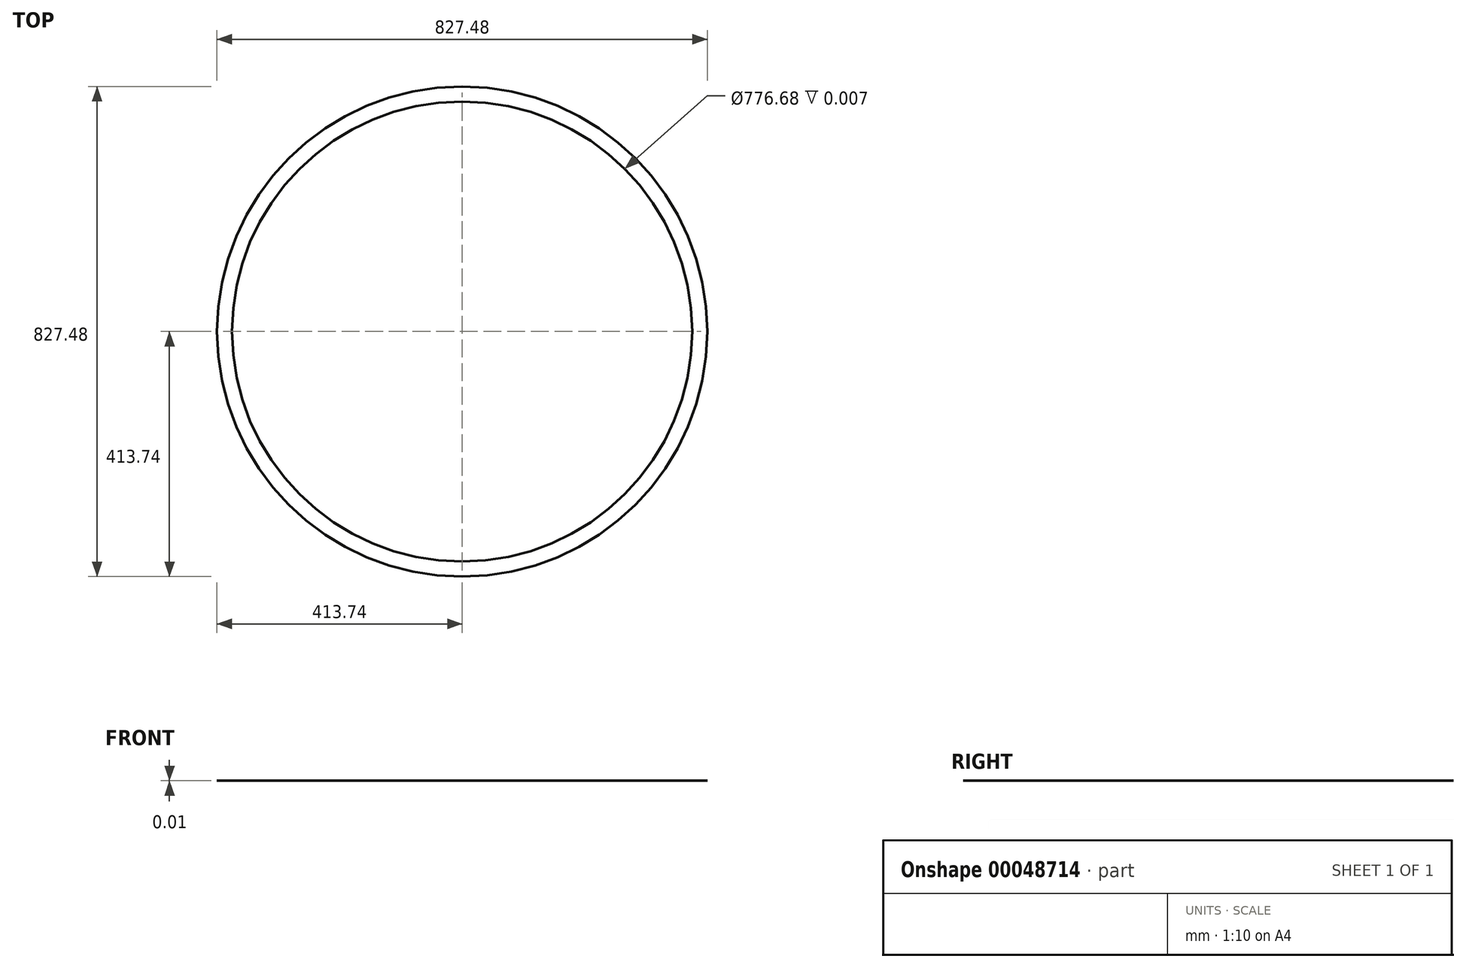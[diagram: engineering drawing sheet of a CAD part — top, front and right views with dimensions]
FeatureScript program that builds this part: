
annotation { "Feature Type Name" : "Feature", "Feature Type Description" : "" }
export const myFeature = defineFeature(function(context is Context, id is Id, definition is map)
    precondition{}
    {
        {
            var Q0;
            Q0=qCreatedBy(makeId("Top.planeOp"),FACE);
            var sketch = newSketch(context, id + "F0", { "sketchPlane" : qUnion([Q0])});
            skCircle(sketch, "E0", {"center": v(0, 0) * mm, "radius": 413.74 * mm});
            skCircle(sketch, "E1", {"center": v(0, 0) * mm, "radius": 388.34 * mm});
            skSolve(sketch);
        }
        {
            var Q0;
            Q0=makeQuery(id+"F0.imprint","IMPRINT",FACE,{"disambiguationData":[TD([[makeQuery(id+"F0.imprint","IMPRINT",EDGE,{"derivedFrom":sQuery(id+"F0.wireOp",EDGE,"E0")}),1.0]])]});
            extrude(context, id + "F1", {"entities" : qUnion([Q0]), "depth" : 3 / 457.2 * mm});
        }
    });
